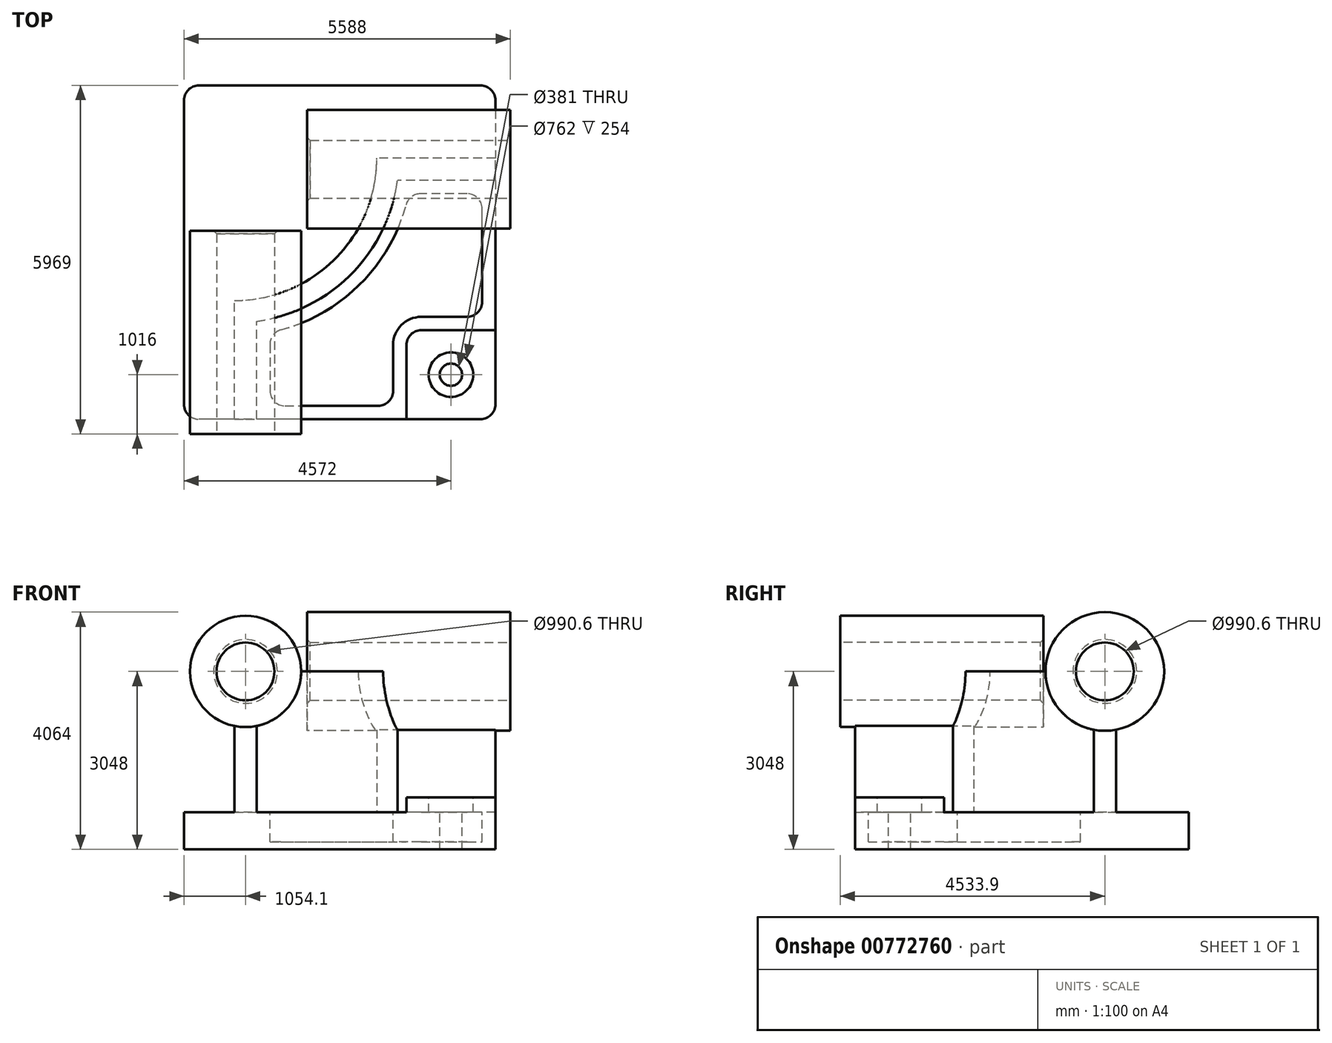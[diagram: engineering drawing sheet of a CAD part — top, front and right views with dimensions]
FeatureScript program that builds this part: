
annotation { "Feature Type Name" : "Feature", "Feature Type Description" : "" }
export const myFeature = defineFeature(function(context is Context, id is Id, definition is map)
    precondition{}
    {
        {
            var Q0;
            Q0=qCreatedBy(makeId("Top.planeOp"),FACE);
            var sketch = newSketch(context, id + "F0", { "sketchPlane" : qUnion([Q0])});
            skLineSegment(sketch, "E0.bottom", {"start": v(2667, 2857.5) * mm, "end": v(-2667, 2857.5) * mm});
            skLineSegment(sketch, "E0.top", {"start": v(2667, -2857.5) * mm, "end": v(-2667, -2857.5) * mm});
            skLineSegment(sketch, "E0.left", {"start": v(2667, 2857.5) * mm, "end": v(2667, -2857.5) * mm});
            skLineSegment(sketch, "E0.right", {"start": v(-2667, 2857.5) * mm, "end": v(-2667, -2857.5) * mm});
            skPoint(sketch, "E0.middle", {"position": v(0, 0) * mm});
            skSolve(sketch);
        }
        {
            var Q0;
            Q0=makeQuery(id+"F0.imprint","IMPRINT",FACE,{"disambiguationData":[TD([[makeQuery(id+"F0.imprint","IMPRINT",EDGE,{"derivedFrom":sQuery(id+"F0.wireOp",EDGE,"E0.bottom")}),1.0]])]});
            extrude(context, id + "F1", {"entities" : qUnion([Q0]), "depth" : 635 * mm, "offsetDistance" : 25.4 * mm});
        }
        {
            var Q0;
            Q0=makeQuery(id+"F1.opExtrude","CAP_FACE",FACE,{"disambiguationData":[OSD([sQuery(id+"F0.wireOp",EDGE,"E0.bottom"),sQuery(id+"F0.wireOp",EDGE,"E0.top"),sQuery(id+"F0.wireOp",EDGE,"E0.left"),sQuery(id+"F0.wireOp",EDGE,"E0.right")])],"isStart":false});
            var sketch = newSketch(context, id + "F2", { "sketchPlane" : qUnion([Q0])});
            skLineSegment(sketch, "E1", {"start": v(-1803.4, -2857.5) * mm, "end": v(-1803.4, -825.5) * mm});
            skLineSegment(sketch, "E2", {"start": v(2667, 1612.9) * mm, "end": v(635, 1612.9) * mm});
            skArc(sketch, "E3", {"start": v(-1803.4, -825.5) * mm, "mid": v(-79.2, -111.3) * mm, "end": v(635, 1612.9) * mm});
            skLineSegment(sketch, "E4", {"start": v(-1803.4, 1612.9) * mm, "end": v(635, 1612.9) * mm, "construction": true});
            skLineSegment(sketch, "E5", {"start": v(-1803.4, 1612.9) * mm, "end": v(-1803.4, -825.5) * mm, "construction": true});
            skLineSegment(sketch, "E6.0", {"start": v(-1422.4, -2857.5) * mm, "end": v(-1422.4, -1180.64) * mm});
            skArc(sketch, "E6.1", {"start": v(-1422.4, -1180.64) * mm, "mid": v(190.22, -380.72) * mm, "end": v(990.14, 1231.9) * mm});
            skLineSegment(sketch, "E6.2", {"start": v(2667, 1231.9) * mm, "end": v(990.14, 1231.9) * mm});
            skLineSegment(sketch, "E7.0", {"start": v(2667, 2857.5) * mm, "end": v(2667, -2857.5) * mm});
            skLineSegment(sketch, "E8.0", {"start": v(2667, -2857.5) * mm, "end": v(-2667, -2857.5) * mm});
            skSolve(sketch);
        }
        {
            var Q0;
            {var subQ2=sQuery(id+"F2.wireOp",EDGE,"E1");Q0=makeQuery(id+"F2.imprint","IMPRINT",FACE,{"disambiguationData":[TD([[makeQuery(id+"F2.imprint","IMPRINT",EDGE,{"derivedFrom":subQ2}),-1.0]])]});}
            extrude(context, id + "F3", {"entities" : qUnion([Q0]), "operationType" : NewBodyOperationType.ADD, "depth" : 2413 * mm, "offsetDistance" : 25.4 * mm});
        }
        {
            var Q0;
            Q0=makeQuery(id+"F3.boolean.opBoolean","MERGE",FACE,{"derivedFrom":[makeQuery(id+"F1.opExtrude","SWEPT_FACE",FACE,{"disambiguationData":[OSD([sQuery(id+"F0.wireOp",EDGE,"E0.top")])]}),makeQuery(id+"F3.opExtrude","SWEPT_FACE",FACE,{"disambiguationData":[OSD([sQuery(id+"F2.wireOp",EDGE,"E8.0")])]})]});
            var sketch = newSketch(context, id + "F4", { "sketchPlane" : qUnion([Q0])});
            skCircle(sketch, "E9", {"center": v(-1612.9, 3048) * mm, "radius": 952.5 * mm});
            skSolve(sketch);
        }
        {
            var Q0;
            Q0 = qSketchRegion(id + "F4", true);
            extrude(context, id + "F5", {"entities" : qUnion([Q0]), "operationType" : NewBodyOperationType.ADD, "depth" : 254 * mm, "offsetDistance" : 25.4 * mm, "hasSecondDirection" : true, "secondDirectionOppositeDirection" : true, "secondDirectionDepth" : 3225.8 * mm});
        }
        {
            var Q0;
            Q0=makeQuery(id+"F3.boolean.opBoolean","MERGE",FACE,{"derivedFrom":[makeQuery(id+"F1.opExtrude","SWEPT_FACE",FACE,{"disambiguationData":[OSD([sQuery(id+"F0.wireOp",EDGE,"E0.left")])]}),makeQuery(id+"F3.opExtrude","SWEPT_FACE",FACE,{"disambiguationData":[OSD([sQuery(id+"F2.wireOp",EDGE,"E7.0")])]})]});
            var sketch = newSketch(context, id + "F6", { "sketchPlane" : qUnion([Q0])});
            skCircle(sketch, "E10", {"center": v(1422.4, 3048) * mm, "radius": 1016 * mm});
            skSolve(sketch);
        }
        {
            var Q0;
            Q0 = qSketchRegion(id + "F6", true);
            extrude(context, id + "F7", {"entities" : qUnion([Q0]), "operationType" : NewBodyOperationType.ADD, "depth" : 254 * mm, "offsetDistance" : 25.4 * mm, "hasSecondDirection" : true, "secondDirectionOppositeDirection" : true, "secondDirectionDepth" : 3225.8 * mm});
        }
        {
            var Q0;
            {var subQ0=sQuery(id+"F0.wireOp",EDGE,"E0.left");var subQ1=sQuery(id+"F0.wireOp",EDGE,"E0.top");Q0=makeQuery(id+"F3.boolean.opBoolean","SPLIT",FACE,{"disambiguationData":[TD([makeQuery(id+"F3.opExtrude","SWEPT_FACE",FACE,{"disambiguationData":[OSD([sQuery(id+"F2.wireOp",EDGE,"E6.0")])]})])],"derivedFrom":makeQuery(id+"F1.opExtrude","CAP_FACE",FACE,{"disambiguationData":[OSD([sQuery(id+"F0.wireOp",EDGE,"E0.bottom"),subQ1,subQ0,sQuery(id+"F0.wireOp",EDGE,"E0.right")])],"isStart":false})});}
            var sketch = newSketch(context, id + "F8", { "sketchPlane" : qUnion([Q0])});
            skLineSegment(sketch, "E11.bottom", {"start": v(2667, -2857.5) * mm, "end": v(1143, -2857.5) * mm});
            skLineSegment(sketch, "E11.top", {"start": v(2667, -1333.5) * mm, "end": v(1143, -1333.5) * mm});
            skLineSegment(sketch, "E11.left", {"start": v(2667, -2857.5) * mm, "end": v(2667, -1333.5) * mm});
            skLineSegment(sketch, "E11.right", {"start": v(1143, -2857.5) * mm, "end": v(1143, -1333.5) * mm});
            skSolve(sketch);
        }
        {
            var Q0;
            Q0=makeQuery(id+"F8.imprint","IMPRINT",FACE,{"disambiguationData":[TD([[makeQuery(id+"F8.imprint","IMPRINT",EDGE,{"derivedFrom":sQuery(id+"F8.wireOp",EDGE,"E11.bottom")}),-1.0]])]});
            extrude(context, id + "F9", {"entities" : qUnion([Q0]), "operationType" : NewBodyOperationType.ADD, "depth" : 254 * mm, "offsetDistance" : 25.4 * mm});
        }
        {
            var Q0;
            Q0=makeQuery(id+"F9.opExtrude","SWEPT_EDGE",EDGE,{"disambiguationData":[OSD([sQuery(id+"F8.wireOp",EDGE,"E11.top"),sQuery(id+"F8.wireOp",EDGE,"E11.right")])]});
            fillet(context, id + "F10", {"entities" : qUnion([Q0]), "radius" : 254 * mm, "tangentPropagation" : true, "allowEdgeOverflow" : false});
        }
        {
            var Q0;
            {var subQ0=sQuery(id+"F0.wireOp",EDGE,"E0.left");var subQ1=sQuery(id+"F0.wireOp",EDGE,"E0.top");Q0=makeQuery(id+"F3.boolean.opBoolean","SPLIT",FACE,{"disambiguationData":[TD([makeQuery(id+"F3.opExtrude","SWEPT_FACE",FACE,{"disambiguationData":[OSD([sQuery(id+"F2.wireOp",EDGE,"E6.0")])]})])],"derivedFrom":makeQuery(id+"F1.opExtrude","CAP_FACE",FACE,{"disambiguationData":[OSD([sQuery(id+"F0.wireOp",EDGE,"E0.bottom"),subQ1,subQ0,sQuery(id+"F0.wireOp",EDGE,"E0.right")])],"isStart":false})});}
            var sketch = newSketch(context, id + "F11", { "sketchPlane" : qUnion([Q0])});
            skLineSegment(sketch, "E12.0", {"start": v(-1193.8, -1373.52) * mm, "end": v(-1193.8, -2628.9) * mm});
            skArc(sketch, "E12.1", {"start": v(1183.02, 1003.3) * mm, "mid": v(351.86, -542.36) * mm, "end": v(-1193.8, -1373.52) * mm});
            skLineSegment(sketch, "E12.2", {"start": v(-1193.8, -2628.9) * mm, "end": v(914.4, -2628.9) * mm});
            skLineSegment(sketch, "E12.3", {"start": v(2438.4, 1003.3) * mm, "end": v(1183.02, 1003.3) * mm});
            skLineSegment(sketch, "E12.4", {"start": v(914.4, -2628.9) * mm, "end": v(914.4, -1587.5) * mm});
            skArc(sketch, "E12.5", {"start": v(914.4, -1587.5) * mm, "mid": v(1055.75, -1246.25) * mm, "end": v(1397, -1104.9) * mm});
            skLineSegment(sketch, "E12.6", {"start": v(1397, -1104.9) * mm, "end": v(2438.4, -1104.9) * mm});
            skLineSegment(sketch, "E12.7", {"start": v(2438.4, -1104.9) * mm, "end": v(2438.4, 1003.3) * mm});
            skSolve(sketch);
        }
        {
            var Q0;
            Q0 = qSketchRegion(id + "F11", true);
            extrude(context, id + "F12", {"entities" : qUnion([Q0]), "operationType" : NewBodyOperationType.REMOVE, "oppositeDirection" : true, "depth" : 508 * mm, "offsetDistance" : 25.4 * mm});
        }
        {
            var Q0;
            Q0=makeQuery(id+"F9.opExtrude","CAP_FACE",FACE,{"disambiguationData":[OSD([sQuery(id+"F8.wireOp",EDGE,"E11.bottom"),sQuery(id+"F8.wireOp",EDGE,"E11.top"),sQuery(id+"F8.wireOp",EDGE,"E11.left"),sQuery(id+"F8.wireOp",EDGE,"E11.right")])],"isStart":false});
            var sketch = newSketch(context, id + "F13", { "sketchPlane" : qUnion([Q0])});
            skCircle(sketch, "E13", {"center": v(1905, -2095.5) * mm, "radius": 381 * mm});
            skSolve(sketch);
        }
        {
            var Q0;
            Q0=sQuery(id+"F13.wireOp",VERTEX,"E13.center");
            var Q1;
            Q1=makeQuery(id+"F1.opExtrude","SWEPT_BODY",BODY,{"disambiguationData":[OSD([sQuery(id+"F0.wireOp",EDGE,"E0.bottom"),sQuery(id+"F0.wireOp",EDGE,"E0.top"),sQuery(id+"F0.wireOp",EDGE,"E0.left"),sQuery(id+"F0.wireOp",EDGE,"E0.right")])]});
            hole(context, id + "F14", {"style" : HoleStyle.C_BORE, "endStyle" : HoleEndStyle.THROUGH, "holeDiameter" : 381 * mm, "cBoreDiameter" : 762 * mm, "cBoreDepth" : 254 * mm, "majorDiameter" : 6.35 * mm, "isTappedThrough" : true, "tappedDepth" : 12.7 * mm, "tapClearance" : 3, "locations" : qUnion([Q0]), "scope" : qUnion([Q1])});
        }
        {
            var Q0;
            Q0=makeQuery(id+"F12.boolean.opBoolean","COPY",EDGE,{"derivedFrom":makeQuery(id+"F12.opExtrude","SWEPT_EDGE",EDGE,{"disambiguationData":[OSD([sQuery(id+"F11.wireOp",EDGE,"E12.1"),sQuery(id+"F11.wireOp",EDGE,"E12.3")])]})});
            var Q1;
            Q1=makeQuery(id+"F12.boolean.opBoolean","COPY",EDGE,{"derivedFrom":makeQuery(id+"F12.opExtrude","SWEPT_EDGE",EDGE,{"disambiguationData":[OSD([sQuery(id+"F11.wireOp",EDGE,"E12.0"),sQuery(id+"F11.wireOp",EDGE,"E12.1")])]})});
            var Q2;
            Q2=makeQuery(id+"F12.boolean.opBoolean","COPY",EDGE,{"derivedFrom":makeQuery(id+"F12.opExtrude","SWEPT_EDGE",EDGE,{"disambiguationData":[OSD([sQuery(id+"F11.wireOp",EDGE,"E12.3"),sQuery(id+"F11.wireOp",EDGE,"E12.7")])]})});
            var Q3;
            Q3=makeQuery(id+"F12.boolean.opBoolean","COPY",EDGE,{"derivedFrom":makeQuery(id+"F12.opExtrude","SWEPT_EDGE",EDGE,{"disambiguationData":[OSD([sQuery(id+"F11.wireOp",EDGE,"E12.0"),sQuery(id+"F11.wireOp",EDGE,"E12.2")])]})});
            var Q4;
            Q4=makeQuery(id+"F12.boolean.opBoolean","COPY",EDGE,{"derivedFrom":makeQuery(id+"F12.opExtrude","SWEPT_EDGE",EDGE,{"disambiguationData":[OSD([sQuery(id+"F11.wireOp",EDGE,"E12.6"),sQuery(id+"F11.wireOp",EDGE,"E12.7")])]})});
            var Q5;
            Q5=makeQuery(id+"F12.boolean.opBoolean","COPY",EDGE,{"derivedFrom":makeQuery(id+"F12.opExtrude","SWEPT_EDGE",EDGE,{"disambiguationData":[OSD([sQuery(id+"F11.wireOp",EDGE,"E12.2"),sQuery(id+"F11.wireOp",EDGE,"E12.4")])]})});
            fillet(context, id + "F15", {"entities" : qUnion([Q0, Q1, Q2, Q3, Q4, Q5]), "radius" : 254 * mm, "tangentPropagation" : true, "allowEdgeOverflow" : false});
        }
        {
            var Q0;
            Q0=makeQuery(id+"F5.opExtrude","CAP_FACE",FACE,{"disambiguationData":[OSD([sQuery(id+"F4.wireOp",EDGE,"E9")])],"isStart":false});
            var sketch = newSketch(context, id + "F16", { "sketchPlane" : qUnion([Q0])});
            skCircle(sketch, "E14", {"center": v(-1612.9, 3048) * mm, "radius": 495.3 * mm});
            skSolve(sketch);
        }
        {
            var Q0;
            Q0=makeQuery(id+"F16.imprint","IMPRINT",FACE,{"disambiguationData":[TD([[makeQuery(id+"F16.imprint","IMPRINT",EDGE,{"derivedFrom":sQuery(id+"F16.wireOp",EDGE,"E14")}),1.0]])]});
            extrude(context, id + "F17", {"entities" : qUnion([Q0]), "operationType" : NewBodyOperationType.REMOVE, "endBound" : BoundingType.THROUGH_ALL, "oppositeDirection" : true, "depth" : 25.4 * mm, "offsetDistance" : 25.4 * mm});
        }
        {
            var Q0;
            Q0=makeQuery(id+"F7.opExtrude","CAP_FACE",FACE,{"disambiguationData":[OSD([sQuery(id+"F6.wireOp",EDGE,"E10")])],"isStart":false});
            var sketch = newSketch(context, id + "F18", { "sketchPlane" : qUnion([Q0])});
            skCircle(sketch, "E15", {"center": v(1422.4, 3048) * mm, "radius": 495.3 * mm});
            skSolve(sketch);
        }
        {
            var Q0;
            Q0 = qSketchRegion(id + "F18", true);
            extrude(context, id + "F19", {"entities" : qUnion([Q0]), "operationType" : NewBodyOperationType.REMOVE, "endBound" : BoundingType.THROUGH_ALL, "oppositeDirection" : true, "depth" : 25.4 * mm, "offsetDistance" : 25.4 * mm});
        }
        {
            var Q0;
            Q0=makeQuery(id+"F19.boolean.opBoolean","COPY",EDGE,{"derivedFrom":makeQuery(id+"F19.opExtrude","CAP_EDGE",EDGE,{"disambiguationData":[OSD([sQuery(id+"F18.wireOp",EDGE,"E15")])],"isStart":true})});
            var Q1;
            Q1=makeQuery(id+"F17.boolean.opBoolean","COPY",EDGE,{"derivedFrom":makeQuery(id+"F17.opExtrude","CAP_EDGE",EDGE,{"disambiguationData":[OSD([sQuery(id+"F16.wireOp",EDGE,"E14")])],"isStart":true})});
            var Q2;
            Q2=makeQuery(id+"F17.boolean.opBoolean","INTERSECT",EDGE,{"derivedFrom":[makeQuery(id+"F5.opExtrude","CAP_FACE",FACE,{"disambiguationData":[OSD([sQuery(id+"F4.wireOp",EDGE,"E9")])],"isStart":true}),makeQuery(id+"F17.opExtrude","SWEPT_FACE",FACE,{"disambiguationData":[OSD([sQuery(id+"F16.wireOp",EDGE,"E14")])]})]});
            var Q3;
            Q3=makeQuery(id+"F19.boolean.opBoolean","INTERSECT",EDGE,{"derivedFrom":[makeQuery(id+"F7.opExtrude","CAP_FACE",FACE,{"disambiguationData":[OSD([sQuery(id+"F6.wireOp",EDGE,"E10")])],"isStart":true}),makeQuery(id+"F19.opExtrude","SWEPT_FACE",FACE,{"disambiguationData":[OSD([sQuery(id+"F18.wireOp",EDGE,"E15")])]})]});
            chamfer(context, id + "F20", {"entities" : qUnion([Q0, Q1, Q2, Q3]), "width" : 50.8 * mm, "tangentPropagation" : true});
        }
        {
            var Q0;
            Q0=makeQuery(id+"F1.opExtrude","SWEPT_EDGE",EDGE,{"disambiguationData":[OSD([sQuery(id+"F0.wireOp",EDGE,"E0.top"),sQuery(id+"F0.wireOp",EDGE,"E0.right")])]});
            var Q1;
            Q1=makeQuery(id+"F9.boolean.opBoolean","MERGE",EDGE,{"derivedFrom":[makeQuery(id+"F1.opExtrude","SWEPT_EDGE",EDGE,{"disambiguationData":[OSD([sQuery(id+"F0.wireOp",EDGE,"E0.top"),sQuery(id+"F0.wireOp",EDGE,"E0.left")])]}),makeQuery(id+"F9.opExtrude","SWEPT_EDGE",EDGE,{"disambiguationData":[OSD([sQuery(id+"F8.wireOp",EDGE,"E11.bottom"),sQuery(id+"F8.wireOp",EDGE,"E11.left")])]})]});
            var Q2;
            Q2=makeQuery(id+"F1.opExtrude","SWEPT_EDGE",EDGE,{"disambiguationData":[OSD([sQuery(id+"F0.wireOp",EDGE,"E0.bottom"),sQuery(id+"F0.wireOp",EDGE,"E0.left")])]});
            var Q3;
            Q3=makeQuery(id+"F1.opExtrude","SWEPT_EDGE",EDGE,{"disambiguationData":[OSD([sQuery(id+"F0.wireOp",EDGE,"E0.bottom"),sQuery(id+"F0.wireOp",EDGE,"E0.right")])]});
            fillet(context, id + "F21", {"entities" : qUnion([Q0, Q1, Q2, Q3]), "radius" : 254 * mm, "tangentPropagation" : true, "allowEdgeOverflow" : false});
        }
    });
